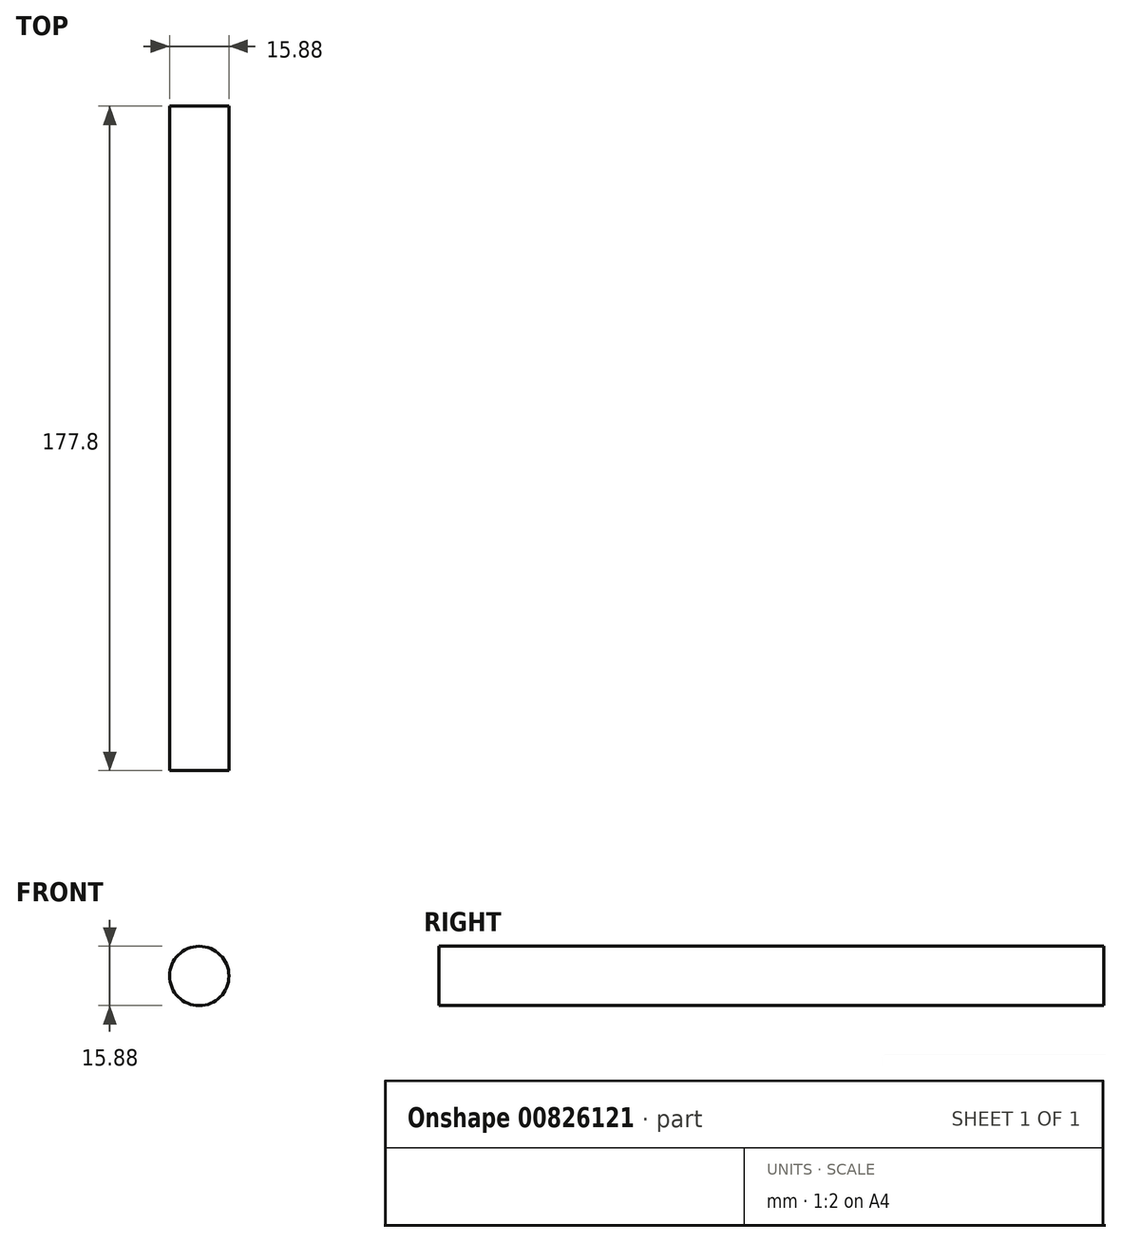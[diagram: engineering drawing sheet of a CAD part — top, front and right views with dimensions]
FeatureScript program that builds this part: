
annotation { "Feature Type Name" : "Feature", "Feature Type Description" : "" }
export const myFeature = defineFeature(function(context is Context, id is Id, definition is map)
    precondition{}
    {
        {
            var Q0;
            Q0=qCreatedBy(makeId("Front.planeOp"),FACE);
            var sketch = newSketch(context, id + "F0", { "sketchPlane" : qUnion([Q0])});
            skCircle(sketch, "E0", {"center": v(0, 0) * mm, "radius": 7.94 * mm});
            skSolve(sketch);
        }
        {
            var Q0;
            Q0=qSketchRegion(id+"F0",true);
            extrude(context, id + "F1", {"entities" : qUnion([Q0]), "endBound" : BoundingType.SYMMETRIC, "depth" : 177.8 * mm, "offsetDistance" : 25.4 * mm});
        }
    });
